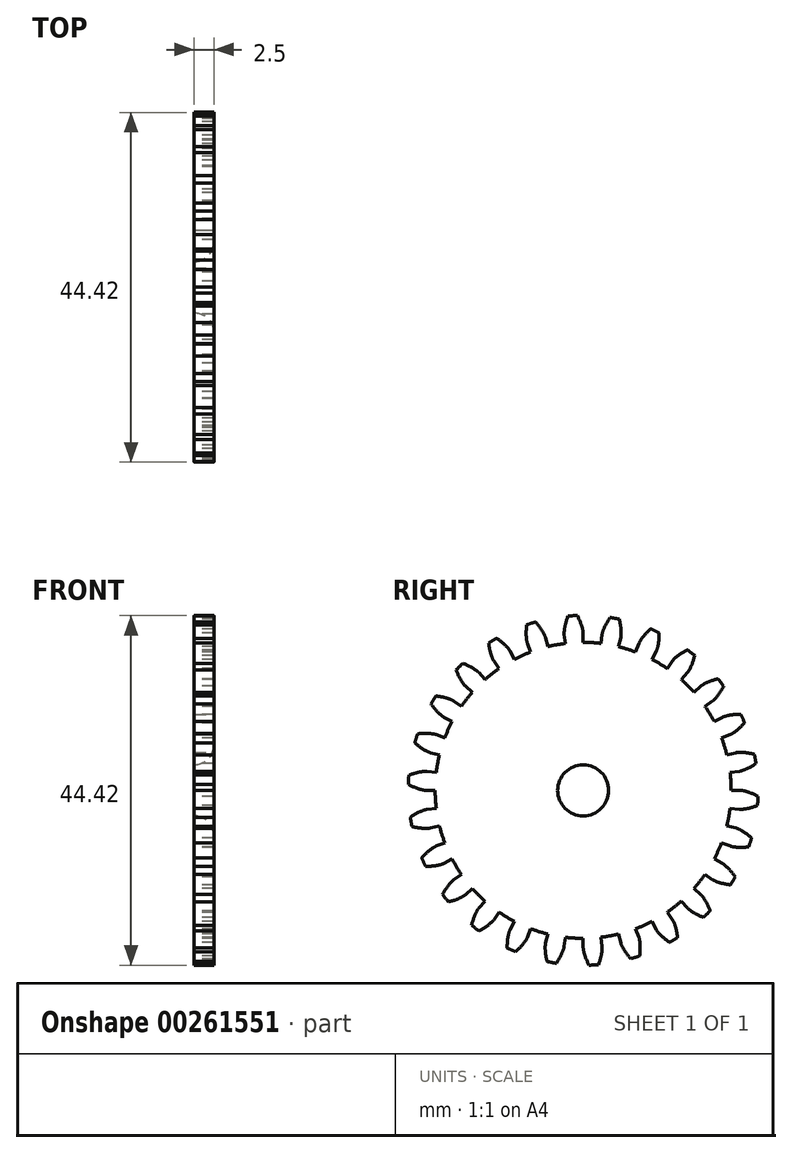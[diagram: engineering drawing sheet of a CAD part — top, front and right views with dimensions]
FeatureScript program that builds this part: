
annotation { "Feature Type Name" : "Feature", "Feature Type Description" : "" }
export const myFeature = defineFeature(function(context is Context, id is Id, definition is map)
    precondition{}
    {
        {
            assignVariable(context, id + "F0", {"name" : "NumberTeeth", "anyValue" : 26});
        }
        {
            assignVariable(context, id + "F1", {"name" : "GearThickness", "anyValue" : 2.5});
        }
        {
            var Q0;
            Q0=qCreatedBy(makeId("Right.planeOp"),FACE);
            var sketch = newSketch(context, id + "F2", { "sketchPlane" : qUnion([Q0])});
            skCircle(sketch, "E0", {"center": v(0, 0) * mm, "radius": 18.8 * mm});
            skCircle(sketch, "E1", {"center": v(0, 0) * mm, "radius": 19.98 * mm, "construction": true});
            skCircle(sketch, "E2", {"center": v(0, 0) * mm, "radius": 20.64 * mm, "construction": true});
            skCircle(sketch, "E3", {"center": v(0, 0) * mm, "radius": 22.23 * mm});
            skLineSegment(sketch, "E4", {"start": v(0, 0) * mm, "end": v(-19.98, 0) * mm, "construction": true});
            skLineSegment(sketch, "E5.1.0", {"start": v(0, 0) * mm, "end": v(-19.96, 1) * mm, "construction": true});
            skLineSegment(sketch, "E5.2.0", {"start": v(0, 0) * mm, "end": v(-19.88, 2) * mm, "construction": true});
            skLineSegment(sketch, "E5.3.0", {"start": v(0, 0) * mm, "end": v(-19.76, 2.99) * mm, "construction": true});
            skLineSegment(sketch, "E5.4.0", {"start": v(0, 0) * mm, "end": v(-19.58, 3.97) * mm, "construction": true});
            skLineSegment(sketch, "E5.5.0", {"start": v(0, 0) * mm, "end": v(-19.36, 4.94) * mm, "construction": true});
            skLineSegment(sketch, "E5.6.0", {"start": v(0, 0) * mm, "end": v(-19.09, 5.9) * mm, "construction": true});
            skLineSegment(sketch, "E5.7.0", {"start": v(0, 0) * mm, "end": v(-18.77, 6.85) * mm, "construction": true});
            skLineSegment(sketch, "E5.8.0", {"start": v(0, 0) * mm, "end": v(-18.4, 7.78) * mm, "construction": true});
            skLineSegment(sketch, "E5.9.0", {"start": v(0, 0) * mm, "end": v(-18, 8.7) * mm, "construction": true});
            skLineSegment(sketch, "E5.10.0", {"start": v(0, 0) * mm, "end": v(-17.53, 9.58) * mm, "construction": true});
            skLineSegment(sketch, "E5.11.0", {"start": v(0, 0) * mm, "end": v(-17.03, 10.44) * mm, "construction": true});
            skLineSegment(sketch, "E5.12.0", {"start": v(0, 0) * mm, "end": v(-16.5, 11.28) * mm, "construction": true});
            skLineSegment(sketch, "E5.13.0", {"start": v(0, 0) * mm, "end": v(-15.9, 12.1) * mm, "construction": true});
            skLineSegment(sketch, "E5.14.0", {"start": v(0, 0) * mm, "end": v(-15.28, 12.87) * mm, "construction": true});
            skLineSegment(sketch, "E5.anchor2", {"start": v(0, 0) * mm, "end": v(-15.28, 12.87) * mm, "construction": true});
            skLineSegment(sketch, "E6", {"start": v(-19.96, 1) * mm, "end": v(-20, 0) * mm, "construction": true});
            skLineSegment(sketch, "E7", {"start": v(-19.88, 2) * mm, "end": v(-20.08, 0) * mm, "construction": true});
            skLineSegment(sketch, "E8", {"start": v(-19.76, 2.99) * mm, "end": v(-20.2, 0.02) * mm, "construction": true});
            skLineSegment(sketch, "E9", {"start": v(-19.36, 4.94) * mm, "end": v(-20.6, 0.1) * mm, "construction": true});
            skLineSegment(sketch, "E10", {"start": v(-19.09, 5.9) * mm, "end": v(-20.86, 0.18) * mm, "construction": true});
            skLineSegment(sketch, "E11", {"start": v(-18.77, 6.85) * mm, "end": v(-21.17, 0.28) * mm, "construction": true});
            skLineSegment(sketch, "E12", {"start": v(-18.4, 7.78) * mm, "end": v(-21.52, 0.42) * mm, "construction": true});
            skLineSegment(sketch, "E13", {"start": v(-18, 8.7) * mm, "end": v(-21.9, 0.6) * mm, "construction": true});
            skLineSegment(sketch, "E14", {"start": v(-17.53, 9.58) * mm, "end": v(-22.32, 0.81) * mm, "construction": true});
            skLineSegment(sketch, "E15", {"start": v(-17.03, 10.44) * mm, "end": v(-22.78, 1.07) * mm, "construction": true});
            skLineSegment(sketch, "E16", {"start": v(-19.58, 3.97) * mm, "end": v(-20.38, 0.05) * mm, "construction": true});
            skLineSegment(sketch, "E17", {"start": v(-16.5, 11.28) * mm, "end": v(-23.26, 1.39) * mm, "construction": true});
            skLineSegment(sketch, "E18", {"start": v(-15.9, 12.1) * mm, "end": v(-23.77, 1.75) * mm, "construction": true});
            skLineSegment(sketch, "E19", {"start": v(-15.28, 12.87) * mm, "end": v(-24.3, 2.17) * mm, "construction": true});
            skLineSegment(sketch, "E20", {"start": v(0, 0) * mm, "end": v(-19.94, 1.2) * mm, "construction": true});
            skLineSegment(sketch, "E21", {"start": v(-18.8, 0) * mm, "end": v(-19.98, 0) * mm});
            skLineSegment(sketch, "E22.MirrorCS", {"start": v(-18.66, 2.27) * mm, "end": v(-19.83, 2.4) * mm});
            skFitSpline(sketch, "E23", {"points": [v(-19.98, 0) * mm, v(-20, 0) * mm, v(-20.08, 0) * mm, v(-20.2, 0.02) * mm, v(-20.38, 0.05) * mm, v(-20.6, 0.1) * mm, v(-20.86, 0.18) * mm, v(-21.17, 0.28) * mm, v(-21.52, 0.42) * mm, v(-21.9, 0.6) * mm, v(-22.32, 0.81) * mm, v(-22.78, 1.07) * mm, v(-23.26, 1.39) * mm, v(-23.77, 1.75) * mm, v(-24.3, 2.17) * mm], "startDerivative": vector(-0.78, 0) * mm, "endDerivative": vector(-1.32, 1.11) * mm});
            skLineSegment(sketch, "E24", {"start": v(-21.12, -0.5) * mm, "end": v(-24.3, 2.17) * mm, "construction": true});
            skFitSpline(sketch, "E25.MirrorCS", {"points": [v(-19.83, 2.4) * mm, v(-19.86, 2.41) * mm, v(-19.93, 2.41) * mm, v(-20.06, 2.41) * mm, v(-20.23, 2.4) * mm, v(-20.46, 2.38) * mm, v(-20.73, 2.34) * mm, v(-21.05, 2.27) * mm, v(-21.4, 2.18) * mm, v(-21.81, 2.05) * mm, v(-22.26, 1.88) * mm, v(-22.74, 1.68) * mm, v(-23.26, 1.43) * mm, v(-23.8, 1.12) * mm, v(-24.38, 0.77) * mm], "startDerivative": vector(-0.78, 0.1) * mm, "endDerivative": vector(-1.45, -0.95) * mm});
            skSolve(sketch);
        }
        {
            var Q0;
            {var subQ0=sQuery(id+"F2.wireOp",EDGE,"E0");var subQ27=makeQuery(id+"F2.imprint","INTERSECT",VERTEX,{"derivedFrom":[subQ0,sQuery(id+"F2.wireOp",EDGE,"10ea1024-8cf5-41f5-a75f-a634b86921f3.10.0")]});Q0=makeQuery(id+"F2.imprint","IMPRINT",FACE,{"disambiguationData":[TD([[makeQuery(id+"F2.imprint","IMPRINT",EDGE,{"disambiguationData":[TD([[subQ27,-1.0]])],"derivedFrom":subQ0}),1.0]])]});}
            var Q1;
            {var subQ0=sQuery(id+"F2.wireOp",EDGE,"10ea1024-8cf5-41f5-a75f-a634b86921f3.1.0");Q1=makeQuery(id+"F2.imprint","IMPRINT",FACE,{"disambiguationData":[TD([[makeQuery(id+"F2.imprint","IMPRINT",EDGE,{"derivedFrom":subQ0}),-1.0]])]});}
            var Q2;
            {var subQ7=sQuery(id+"F2.wireOp",EDGE,"10ea1024-8cf5-41f5-a75f-a634b86921f3.2.0");Q2=makeQuery(id+"F2.imprint","IMPRINT",FACE,{"disambiguationData":[TD([[makeQuery(id+"F2.imprint","IMPRINT",EDGE,{"derivedFrom":subQ7}),-1.0]])]});}
            var Q3;
            {var subQ8=sQuery(id+"F2.wireOp",EDGE,"10ea1024-8cf5-41f5-a75f-a634b86921f3.3.0");Q3=makeQuery(id+"F2.imprint","IMPRINT",FACE,{"disambiguationData":[TD([[makeQuery(id+"F2.imprint","IMPRINT",EDGE,{"derivedFrom":subQ8}),-1.0]])]});}
            var Q4;
            {var subQ2=sQuery(id+"F2.wireOp",EDGE,"10ea1024-8cf5-41f5-a75f-a634b86921f3.4.0");Q4=makeQuery(id+"F2.imprint","IMPRINT",FACE,{"disambiguationData":[TD([[makeQuery(id+"F2.imprint","IMPRINT",EDGE,{"derivedFrom":subQ2}),-1.0]])]});}
            var Q5;
            {var subQ8=sQuery(id+"F2.wireOp",EDGE,"10ea1024-8cf5-41f5-a75f-a634b86921f3.5.0");Q5=makeQuery(id+"F2.imprint","IMPRINT",FACE,{"disambiguationData":[TD([[makeQuery(id+"F2.imprint","IMPRINT",EDGE,{"derivedFrom":subQ8}),-1.0]])]});}
            var Q6;
            {var subQ3=sQuery(id+"F2.wireOp",EDGE,"10ea1024-8cf5-41f5-a75f-a634b86921f3.6.0");Q6=makeQuery(id+"F2.imprint","IMPRINT",FACE,{"disambiguationData":[TD([[makeQuery(id+"F2.imprint","IMPRINT",EDGE,{"derivedFrom":subQ3}),-1.0]])]});}
            var Q7;
            {var subQ0=sQuery(id+"F2.wireOp",EDGE,"10ea1024-8cf5-41f5-a75f-a634b86921f3.7.0");Q7=makeQuery(id+"F2.imprint","IMPRINT",FACE,{"disambiguationData":[TD([[makeQuery(id+"F2.imprint","IMPRINT",EDGE,{"derivedFrom":subQ0}),-1.0]])]});}
            var Q8;
            {var subQ5=sQuery(id+"F2.wireOp",EDGE,"10ea1024-8cf5-41f5-a75f-a634b86921f3.8.0");Q8=makeQuery(id+"F2.imprint","IMPRINT",FACE,{"disambiguationData":[TD([[makeQuery(id+"F2.imprint","IMPRINT",EDGE,{"derivedFrom":subQ5}),-1.0]])]});}
            var Q9;
            {var subQ1=sQuery(id+"F2.wireOp",EDGE,"10ea1024-8cf5-41f5-a75f-a634b86921f3.9.0");Q9=makeQuery(id+"F2.imprint","IMPRINT",FACE,{"disambiguationData":[TD([[makeQuery(id+"F2.imprint","IMPRINT",EDGE,{"derivedFrom":subQ1}),-1.0]])]});}
            var Q10;
            {var subQ5=sQuery(id+"F2.wireOp",EDGE,"10ea1024-8cf5-41f5-a75f-a634b86921f3.10.0");Q10=makeQuery(id+"F2.imprint","IMPRINT",FACE,{"disambiguationData":[TD([[makeQuery(id+"F2.imprint","IMPRINT",EDGE,{"derivedFrom":subQ5}),-1.0]])]});}
            var Q11;
            {var subQ8=sQuery(id+"F2.wireOp",EDGE,"10ea1024-8cf5-41f5-a75f-a634b86921f3.11.0");Q11=makeQuery(id+"F2.imprint","IMPRINT",FACE,{"disambiguationData":[TD([[makeQuery(id+"F2.imprint","IMPRINT",EDGE,{"derivedFrom":subQ8}),-1.0]])]});}
            var Q12;
            {var subQ2=sQuery(id+"F2.wireOp",EDGE,"10ea1024-8cf5-41f5-a75f-a634b86921f3.12.0");Q12=makeQuery(id+"F2.imprint","IMPRINT",FACE,{"disambiguationData":[TD([[makeQuery(id+"F2.imprint","IMPRINT",EDGE,{"derivedFrom":subQ2}),-1.0]])]});}
            var Q13;
            {var subQ3=sQuery(id+"F2.wireOp",EDGE,"10ea1024-8cf5-41f5-a75f-a634b86921f3.13.0");Q13=makeQuery(id+"F2.imprint","IMPRINT",FACE,{"disambiguationData":[TD([[makeQuery(id+"F2.imprint","IMPRINT",EDGE,{"derivedFrom":subQ3}),-1.0]])]});}
            var Q14;
            {var subQ0=sQuery(id+"F2.wireOp",EDGE,"10ea1024-8cf5-41f5-a75f-a634b86921f3.14.0");Q14=makeQuery(id+"F2.imprint","IMPRINT",FACE,{"disambiguationData":[TD([[makeQuery(id+"F2.imprint","IMPRINT",EDGE,{"derivedFrom":subQ0}),-1.0]])]});}
            var Q15;
            {var subQ6=sQuery(id+"F2.wireOp",EDGE,"10ea1024-8cf5-41f5-a75f-a634b86921f3.15.0");Q15=makeQuery(id+"F2.imprint","IMPRINT",FACE,{"disambiguationData":[TD([[makeQuery(id+"F2.imprint","IMPRINT",EDGE,{"derivedFrom":subQ6}),-1.0]])]});}
            var Q16;
            {var subQ5=sQuery(id+"F2.wireOp",EDGE,"10ea1024-8cf5-41f5-a75f-a634b86921f3.16.0");Q16=makeQuery(id+"F2.imprint","IMPRINT",FACE,{"disambiguationData":[TD([[makeQuery(id+"F2.imprint","IMPRINT",EDGE,{"derivedFrom":subQ5}),-1.0]])]});}
            var Q17;
            {var subQ7=sQuery(id+"F2.wireOp",EDGE,"10ea1024-8cf5-41f5-a75f-a634b86921f3.17.0");Q17=makeQuery(id+"F2.imprint","IMPRINT",FACE,{"disambiguationData":[TD([[makeQuery(id+"F2.imprint","IMPRINT",EDGE,{"derivedFrom":subQ7}),-1.0]])]});}
            var Q18;
            {var subQ5=sQuery(id+"F2.wireOp",EDGE,"10ea1024-8cf5-41f5-a75f-a634b86921f3.18.0");Q18=makeQuery(id+"F2.imprint","IMPRINT",FACE,{"disambiguationData":[TD([[makeQuery(id+"F2.imprint","IMPRINT",EDGE,{"derivedFrom":subQ5}),-1.0]])]});}
            var Q19;
            {var subQ8=sQuery(id+"F2.wireOp",EDGE,"10ea1024-8cf5-41f5-a75f-a634b86921f3.19.0");Q19=makeQuery(id+"F2.imprint","IMPRINT",FACE,{"disambiguationData":[TD([[makeQuery(id+"F2.imprint","IMPRINT",EDGE,{"derivedFrom":subQ8}),-1.0]])]});}
            var Q20;
            {var subQ8=sQuery(id+"F2.wireOp",EDGE,"E21");Q20=makeQuery(id+"F2.imprint","IMPRINT",FACE,{"disambiguationData":[TD([[makeQuery(id+"F2.imprint","IMPRINT",EDGE,{"derivedFrom":subQ8}),-1.0]])]});}
            extrude(context, id + "F3", {"entities" : qUnion([Q0, Q1, Q2, Q3, Q4, Q5, Q6, Q7, Q8, Q9, Q10, Q11, Q12, Q13, Q14, Q15, Q16, Q17, Q18, Q19, Q20]), "depth" : (getVariable(context, 'GearThickness')) * mm});
        }
        {
            var Q0;
            Q0=makeQuery(id+"F3.opExtrude","SWEPT_FACE",FACE,{"disambiguationData":[OSD([sQuery(id+"F2.wireOp",EDGE,"E25.MirrorCS")])]});
            var Q1;
            Q1=makeQuery(id+"F3.opExtrude","SWEPT_FACE",FACE,{"disambiguationData":[OSD([sQuery(id+"F2.wireOp",EDGE,"E23")])]});
            var Q2;
            Q2=makeQuery(id+"F3.opExtrude","SWEPT_FACE",FACE,{"disambiguationData":[OSD([sQuery(id+"F2.wireOp",EDGE,"E3")])]});
            var Q3;
            Q3=makeQuery(id+"F3.opExtrude","SWEPT_FACE",FACE,{"disambiguationData":[OSD([sQuery(id+"F2.wireOp",EDGE,"E22.MirrorCS")])]});
            var Q4;
            Q4=makeQuery(id+"F3.opExtrude","SWEPT_FACE",FACE,{"disambiguationData":[OSD([sQuery(id+"F2.wireOp",EDGE,"E21")])]});
            var Q5;
            Q5=makeQuery(id+"F3.opExtrude","SWEPT_FACE",FACE,{"disambiguationData":[OSD([sQuery(id+"F2.wireOp",EDGE,"E0")])]});
            circularPattern(context, id + "F4", {"faces" : qUnion([Q0, Q1, Q2, Q3, Q4]), "axis" : qUnion([Q5]), "angle" : 360 * degree, "instanceCount" : getVariable(context, 'NumberTeeth'), "equalSpace" : true, "patternType" : PatternType.FACE});
        }
        {
            var Q0;
            Q0=makeQuery(id+"F3.opExtrude","CAP_FACE",FACE,{"disambiguationData":[OSD([sQuery(id+"F2.wireOp",EDGE,"E0"),sQuery(id+"F2.wireOp",EDGE,"E3"),sQuery(id+"F2.wireOp",EDGE,"E21"),sQuery(id+"F2.wireOp",EDGE,"E22.MirrorCS"),sQuery(id+"F2.wireOp",EDGE,"E23"),sQuery(id+"F2.wireOp",EDGE,"E25.MirrorCS")])],"isStart":true});
            var sketch = newSketch(context, id + "F5", { "sketchPlane" : qUnion([Q0])});
            skCircle(sketch, "E26", {"center": v(0, 0) * mm, "radius": 3.24 * mm});
            skSolve(sketch);
        }
        {
            var Q0;
            Q0=makeQuery(id+"F5.imprint","IMPRINT",FACE,{"disambiguationData":[TD([[makeQuery(id+"F5.imprint","IMPRINT",EDGE,{"derivedFrom":sQuery(id+"F5.wireOp",EDGE,"E26")}),1.0]])]});
            extrude(context, id + "F6", {"entities" : qUnion([Q0]), "operationType" : NewBodyOperationType.REMOVE, "endBound" : BoundingType.THROUGH_ALL, "oppositeDirection" : true, "depth" : 25.4 * mm});
        }
        {
            var Q0;
            Q0=qCreatedBy(makeId("Front.planeOp"),FACE);
            cPlane(context, id + "F7", {"entities" : qUnion([Q0]), "cplaneType" : CPlaneType.OFFSET, "offset" : 25.4 * mm, "width" : 152.4 * mm, "height" : 152.4 * mm});
        }
        {
            var Q0;
            Q0=qCreatedBy(id+"F7.planeOp",FACE);
            var sketch = newSketch(context, id + "F8", { "sketchPlane" : qUnion([Q0])});
            skCircle(sketch, "E27", {"center": v(10.16, 0) * mm, "radius": 2.35 * mm});
            skSolve(sketch);
        }
        {
            var Q0;
            Q0=makeQuery(id+"F8.imprint","IMPRINT",FACE,{"disambiguationData":[TD([[makeQuery(id+"F8.imprint","IMPRINT",EDGE,{"derivedFrom":sQuery(id+"F8.wireOp",EDGE,"E27")}),1.0]])]});
            extrude(context, id + "F9", {"entities" : qUnion([Q0]), "operationType" : NewBodyOperationType.REMOVE, "endBound" : BoundingType.THROUGH_ALL, "oppositeDirection" : true, "depth" : 25.4 * mm});
        }
        {
            var Q0;
            Q0=makeQuery(id+"F6.boolean.opBoolean","COPY",EDGE,{"derivedFrom":makeQuery(id+"F6.opExtrude","CAP_EDGE",EDGE,{"disambiguationData":[OSD([sQuery(id+"F5.wireOp",EDGE,"E26")])],"isStart":true})});
            var Q1;
            Q1=makeQuery(id+"F6.boolean.opBoolean","INTERSECT",EDGE,{"derivedFrom":[makeQuery(id+"F3.opExtrude","CAP_FACE",FACE,{"disambiguationData":[OSD([sQuery(id+"F2.wireOp",EDGE,"E0"),sQuery(id+"F2.wireOp",EDGE,"E3"),sQuery(id+"F2.wireOp",EDGE,"E21"),sQuery(id+"F2.wireOp",EDGE,"E22.MirrorCS"),sQuery(id+"F2.wireOp",EDGE,"E23"),sQuery(id+"F2.wireOp",EDGE,"E25.MirrorCS")])],"isStart":false}),makeQuery(id+"F6.opExtrude","SWEPT_FACE",FACE,{"disambiguationData":[OSD([sQuery(id+"F5.wireOp",EDGE,"E26")])]})]});
            fillet(context, id + "F10", {"entities" : qUnion([Q0, Q1]), "radius" : 2.54 * mm, "tangentPropagation" : true, "allowEdgeOverflow" : false});
        }
    });
